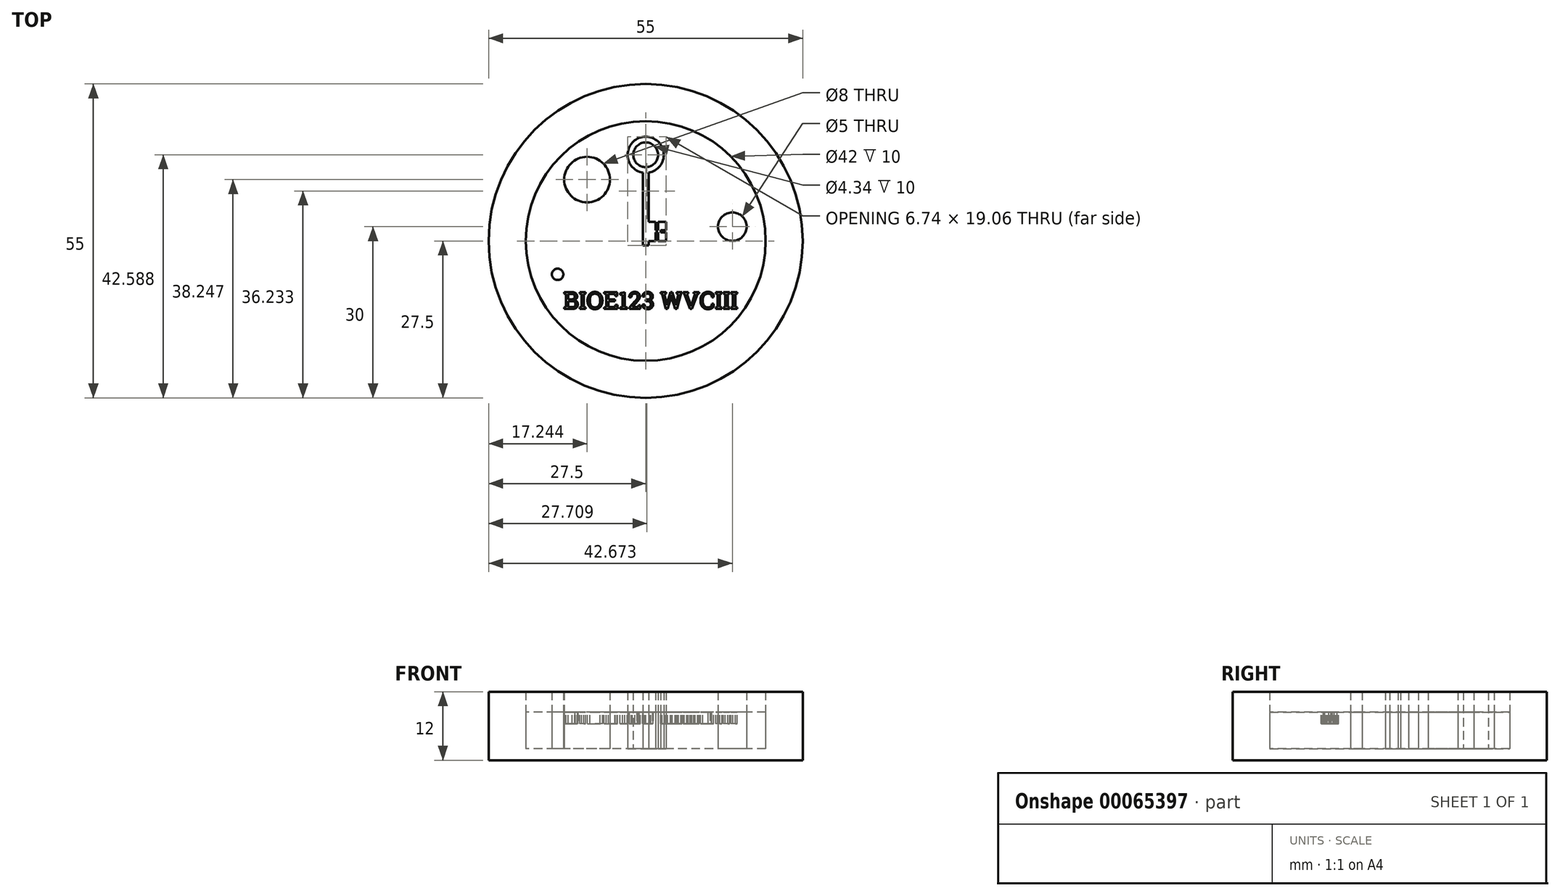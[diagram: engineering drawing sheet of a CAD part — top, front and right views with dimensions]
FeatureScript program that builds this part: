
annotation { "Feature Type Name" : "Feature", "Feature Type Description" : "" }
export const myFeature = defineFeature(function(context is Context, id is Id, definition is map)
    precondition{}
    {
        {
            var Q0;
            Q0=qCreatedBy(makeId("Top.planeOp"),FACE);
            var sketch = newSketch(context, id + "F0", { "sketchPlane" : qUnion([Q0])});
            skCircle(sketch, "E0", {"center": v(0, 0) * mm, "radius": 21 * mm});
            skCircle(sketch, "E1", {"center": v(0, 0) * mm, "radius": 27.5 * mm});
            skCircle(sketch, "E2", {"center": v(-15.42, -5.85) * mm, "radius": 1 * mm});
            skCircle(sketch, "E3", {"center": v(-10.26, 10.75) * mm, "radius": 4 * mm});
            skCircle(sketch, "E4", {"center": v(15.17, 2.5) * mm, "radius": 2.5 * mm});
            skLineSegment(sketch, "E5", {"start": v(0.5, 3.33) * mm, "end": v(0.5, 11.96) * mm});
            skLineSegment(sketch, "E6", {"start": v(-0.5, 11.96) * mm, "end": v(-0.5, -0.8) * mm});
            skLineSegment(sketch, "E7", {"start": v(-0.5, -0.8) * mm, "end": v(0.5, -0.8) * mm});
            skLineSegment(sketch, "E8", {"start": v(0.5, -0.8) * mm, "end": v(0.5, 0) * mm});
            skLineSegment(sketch, "E9", {"start": v(0.5, 0) * mm, "end": v(1.7, 0) * mm});
            skLineSegment(sketch, "E10", {"start": v(1.7, 0) * mm, "end": v(1.7, 1.47) * mm});
            skLineSegment(sketch, "E11", {"start": v(1.7, 1.47) * mm, "end": v(2.17, 1.47) * mm});
            skLineSegment(sketch, "E12", {"start": v(2.17, 1.47) * mm, "end": v(2.17, 0) * mm});
            skLineSegment(sketch, "E13", {"start": v(2.17, 0) * mm, "end": v(3.58, 0) * mm});
            skLineSegment(sketch, "E14", {"start": v(3.58, 0) * mm, "end": v(3.58, 1.47) * mm});
            skLineSegment(sketch, "E15", {"start": v(3.58, 1.47) * mm, "end": v(2.6, 1.47) * mm});
            skLineSegment(sketch, "E16", {"start": v(2.6, 1.47) * mm, "end": v(2.6, 1.9) * mm});
            skLineSegment(sketch, "E17", {"start": v(2.6, 1.9) * mm, "end": v(3.57, 1.9) * mm});
            skLineSegment(sketch, "E18", {"start": v(3.57, 1.9) * mm, "end": v(3.57, 3.33) * mm});
            skLineSegment(sketch, "E19", {"start": v(3.57, 3.33) * mm, "end": v(2.17, 3.33) * mm});
            skLineSegment(sketch, "E20", {"start": v(2.17, 3.33) * mm, "end": v(2.17, 1.9) * mm});
            skLineSegment(sketch, "E21", {"start": v(2.17, 1.9) * mm, "end": v(1.7, 1.9) * mm});
            skLineSegment(sketch, "E22", {"start": v(1.7, 1.9) * mm, "end": v(1.7, 3.33) * mm});
            skLineSegment(sketch, "E23", {"start": v(1.7, 3.33) * mm, "end": v(0.5, 3.33) * mm});
            skLineSegment(sketch, "E24", {"start": v(0.5, 3.33) * mm, "end": v(0.5, 3.33) * mm});
            skArc(sketch, "E25", {"start": v(-0.5, 11.96) * mm, "mid": v(0, 18.26) * mm, "end": v(0.5, 11.96) * mm});
            skCircle(sketch, "E26", {"center": v(0, 15.09) * mm, "radius": 2.17 * mm});
            skSolve(sketch);
        }
        {
            var Q0;
            Q0 = qSketchRegion(id + "F0", true);
            var Q1;
            Q1=makeQuery(id+"F0.imprint","IMPRINT",FACE,{"disambiguationData":[TD([[makeQuery(id+"F0.imprint","IMPRINT",EDGE,{"derivedFrom":sQuery(id+"F0.wireOp",EDGE,"E0")}),1.0]])]});
            var Q2;
            Q2=makeQuery(id+"F0.imprint","IMPRINT",FACE,{"disambiguationData":[TD([[makeQuery(id+"F0.imprint","IMPRINT",EDGE,{"derivedFrom":sQuery(id+"F0.wireOp",EDGE,"E3")}),1.0]])]});
            var Q3;
            Q3=makeQuery(id+"F0.imprint","IMPRINT",FACE,{"disambiguationData":[TD([[makeQuery(id+"F0.imprint","IMPRINT",EDGE,{"derivedFrom":sQuery(id+"F0.wireOp",EDGE,"E26")}),1.0]])]});
            var Q4;
            Q4=makeQuery(id+"F0.imprint","IMPRINT",FACE,{"disambiguationData":[TD([[makeQuery(id+"F0.imprint","IMPRINT",EDGE,{"derivedFrom":sQuery(id+"F0.wireOp",EDGE,"E5")}),1.0]])]});
            var Q5;
            Q5=makeQuery(id+"F0.imprint","IMPRINT",FACE,{"disambiguationData":[TD([[makeQuery(id+"F0.imprint","IMPRINT",EDGE,{"derivedFrom":sQuery(id+"F0.wireOp",EDGE,"E4")}),1.0]])]});
            var Q6;
            Q6=makeQuery(id+"F0.imprint","IMPRINT",FACE,{"disambiguationData":[TD([[makeQuery(id+"F0.imprint","IMPRINT",EDGE,{"derivedFrom":sQuery(id+"F0.wireOp",EDGE,"E2")}),1.0]])]});
            extrude(context, id + "F1", {"entities" : qUnion([Q0, Q1, Q2, Q3, Q4, Q5, Q6]), "oppositeDirection" : true, "depth" : 2 * mm});
        }
        {
            var Q0;
            Q0 = qSketchRegion(id + "F0", true);
            var Q1;
            Q1=makeQuery(id+"F0.imprint","IMPRINT",FACE,{"disambiguationData":[TD([[makeQuery(id+"F0.imprint","IMPRINT",EDGE,{"derivedFrom":sQuery(id+"F0.wireOp",EDGE,"E3")}),1.0]])]});
            var Q2;
            Q2=makeQuery(id+"F0.imprint","IMPRINT",FACE,{"disambiguationData":[TD([[makeQuery(id+"F0.imprint","IMPRINT",EDGE,{"derivedFrom":sQuery(id+"F0.wireOp",EDGE,"E5")}),1.0]])]});
            var Q3;
            Q3=makeQuery(id+"F0.imprint","IMPRINT",FACE,{"disambiguationData":[TD([[makeQuery(id+"F0.imprint","IMPRINT",EDGE,{"derivedFrom":sQuery(id+"F0.wireOp",EDGE,"E2")}),1.0]])]});
            var Q4;
            Q4=makeQuery(id+"F0.imprint","IMPRINT",FACE,{"disambiguationData":[TD([[makeQuery(id+"F0.imprint","IMPRINT",EDGE,{"derivedFrom":sQuery(id+"F0.wireOp",EDGE,"E4")}),1.0]])]});
            extrude(context, id + "F2", {"entities" : qUnion([Q0, Q1, Q2, Q3, Q4]), "operationType" : NewBodyOperationType.ADD, "depth" : 10 * mm});
        }
        {
            var Q0;
            Q0=makeQuery(id+"F2.boolean.opBoolean","SPLIT",FACE,{"disambiguationData":[TD([makeQuery(id+"F2.opExtrude","SWEPT_FACE",FACE,{"disambiguationData":[OSD([sQuery(id+"F0.wireOp",EDGE,"E0")])]})])],"derivedFrom":makeQuery(id+"F1.opExtrude","CAP_FACE",FACE,{"disambiguationData":[OSD([sQuery(id+"F0.wireOp",EDGE,"E1")])],"isStart":true})});
            extrude(context, id + "F3", {"entities" : qUnion([Q0]), "depth" : 6.4 * mm});
        }
        {
            var Q0;
            Q0=makeQuery(id+"F3.opExtrude","CAP_FACE",FACE,{"disambiguationData":[OSD([sQuery(id+"F0.wireOp",EDGE,"E1")])],"isStart":false});
            var sketch = newSketch(context, id + "F4", { "sketchPlane" : qUnion([Q0])});
            skText(sketch, "E27", { "text": "BIOE123 WVCIII", "fontName": "RobotoSlab-Regular.ttf"});
            const initialGuessF4  = {"E27": [-0.01443, -0.01193, 1, 0, 0.003]};
            skSetInitialGuess(sketch, initialGuessF4);
            skSolve(sketch);
        }
        {
            var Q0;
            Q0 = qSketchRegion(id + "F4", true);
            extrude(context, id + "F5", {"entities" : qUnion([Q0]), "operationType" : NewBodyOperationType.REMOVE, "oppositeDirection" : true, "depth" : 2 * mm});
        }
    });
